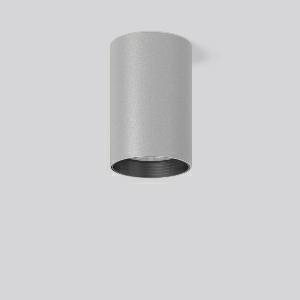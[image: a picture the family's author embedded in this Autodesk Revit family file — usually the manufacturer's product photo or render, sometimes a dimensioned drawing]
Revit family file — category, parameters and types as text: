
# Revit family: heledon_maxi_a_931227_004_1_bada
name_source: partatom
category: Lighting Fixtures
units: mm (PartAtom-declared; Revit-internal decimal feet)

## family parameters
Cut with Voids When Loaded = No
Host = Face
Light Source = No
Part Type = Normal
Room Calculation Point = No
Round Connector Dimension = Use Diameter
Shared = No

## types (1)
- HELEDON maxi A (1 x LED Modul 940, 3900 lm, 4000)
    Apparent Load = 35 VA
    Approval mark = CE
    CIE Flux Codes = 97 100 100 100 100
    Color Rendering = 92
    Color Temperature = 4000
    Default Elevation = 1800 mm
    Description = Series: HELEDON maxi
Cylindrical surface-mounted downlight. Housing: die-cast aluminium, powder-coated. Internal ceiling frame polycarbonate with bayonet mounting. Black plastic ring and recessed LED to prevent glare from the side. Optical assembly with lens made of plastic (polycarbonate) for the best homogeneous light distribution - can be changed without tools. Best colour rendering index Ra>90. Suitable for Ceiling mounting. Easy installation with a separate ceiling frame with bayonet mounting and plug connection. Driver integrated. Connected via plug-in connector. High quality converter without flickering and stroboscopic effect. The following accessories can be mounted without use of tools: interchangeable lenses, decorative glasses, honeycomb louvre, clear and frosted diffusers, white interchangeable plastic ring. 
Colour: silver
Diameter: 123 mm
Height: 183 mm
Lamp: LED
Socket: without socket
Colour temperature: 4000K
Colour rendering index (CRI): 92
System power: 35 W
Rated luminous flux: 3900 lm
Luminous efficiency: 111 lm/W
Control gear: Regulated power supply
Protection class: I
Type of protection: IP 20
    Height = 183 mm
    Lamp = 1 x LED Modul 940
    Lamp Light Flux = 3900 lm
    Lamp count = 1
    Length = 123 mm
    Lifetime = 50000 h
    Luminous efficacy = 111 lm/W
    Manufacturer = RZB
    ModVariant = No
    Model = 931227.004.1
    Mounting Place = Ceiling
    Mounting Type = Surface mounted
    Number of Poles = 1
    OnlyDefault = Yes
    Power Factor = 1
    Product Name = HELEDON maxi A
    Product group = Surface mounted downlights
    ProductGroupID = 302
    Protection Class = Protection class I
    Protection Degree = IP 20
    RLX_Detail_Level = 1
    RLX_Emergency_Light_Flux = 0 lm
    RLX_Emergency_Type = 0
    RLX_Emergency_Type_DB = No
    RlxData = <blob elided: 97605 chars, md5=884bdf13>
    Socket = socket
    Standby Power = 0 W
    System Light Flux = 3900 lm
    System Power = 35 W
    Type Comments = Product without accessories
    Type Image = 931193.004.jpg
    URL = http://relux.com
    VarID = ---
    Voltage = 230 V
    Voltage Range = 220-240 V
    Weight = 0.00 kg
    Width = 0 mm  [stored 0 ft]

note: [stored X ft] marks values corroborated as IEEE doubles in the binary element streams (Revit-internal decimal feet)

## geometry (parser evidence)
native form markers: Blend x4, Sweep x10
no freeform markers — native parametric forms only
